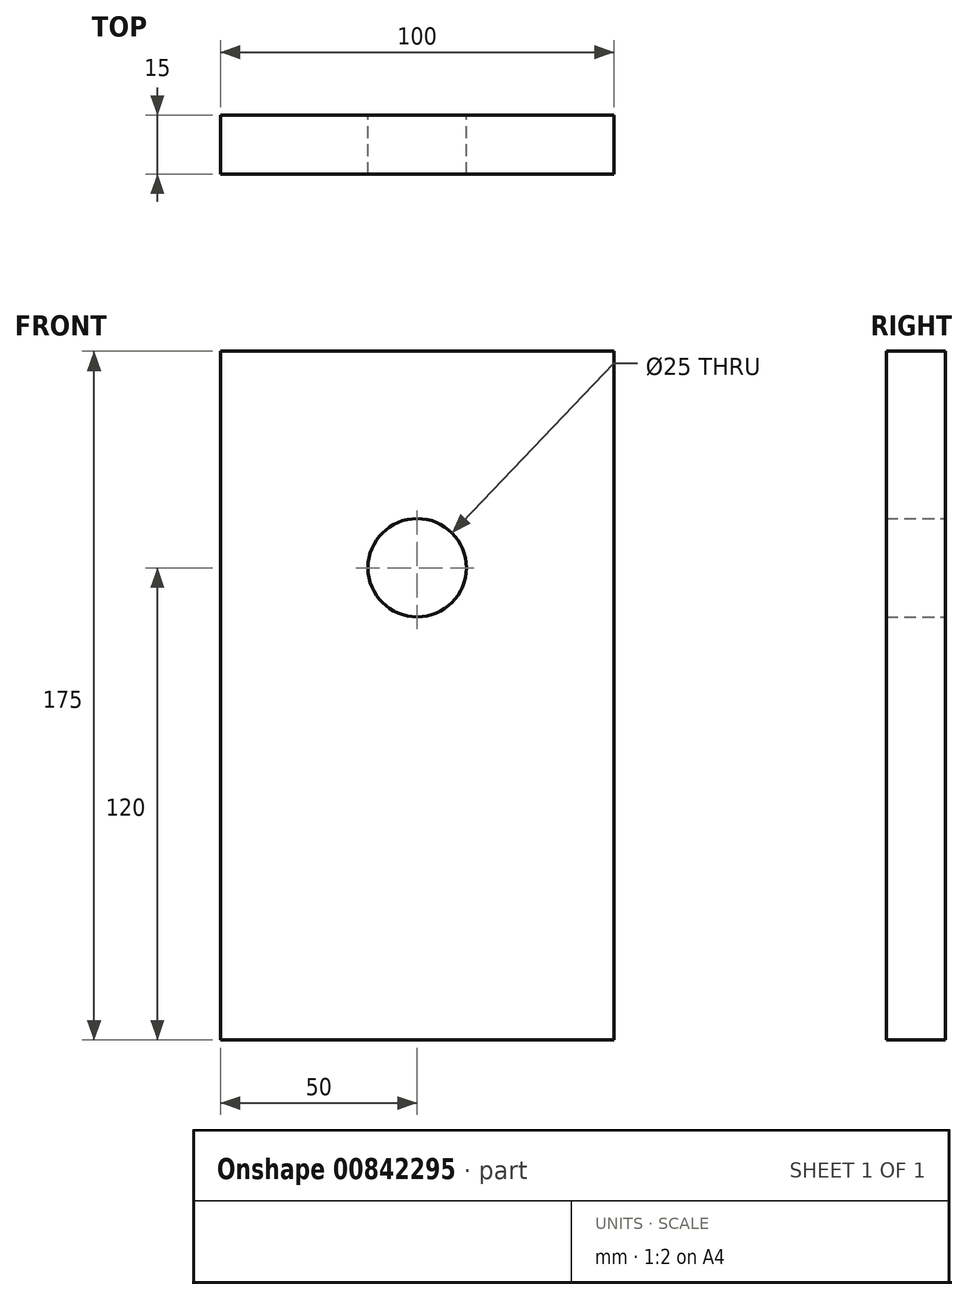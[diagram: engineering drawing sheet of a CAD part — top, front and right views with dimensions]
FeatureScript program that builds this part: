
annotation { "Feature Type Name" : "Feature", "Feature Type Description" : "" }
export const myFeature = defineFeature(function(context is Context, id is Id, definition is map)
    precondition{}
    {
        {
            var Q0;
            Q0=qCreatedBy(makeId("Front.planeOp"),FACE);
            var sketch = newSketch(context, id + "F0", { "sketchPlane" : qUnion([Q0])});
            skLineSegment(sketch, "E0.bottom", {"start": v(50, -87.5) * mm, "end": v(-50, -87.5) * mm});
            skLineSegment(sketch, "E0.top", {"start": v(50, 87.5) * mm, "end": v(-50, 87.5) * mm});
            skLineSegment(sketch, "E0.left", {"start": v(50, -87.5) * mm, "end": v(50, 87.5) * mm});
            skLineSegment(sketch, "E0.right", {"start": v(-50, -87.5) * mm, "end": v(-50, 87.5) * mm});
            skPoint(sketch, "E0.middle", {"position": v(0, 0) * mm});
            skCircle(sketch, "E1", {"center": v(0, 32.5) * mm, "radius": 12.5 * mm});
            skSolve(sketch);
        }
        {
            var Q0;
            Q0 = qSketchRegion(id + "F0", true);
            extrude(context, id + "F1", {"entities" : qUnion([Q0]), "depth" : 15 * mm, "offsetDistance" : 25 * mm});
        }
    });
